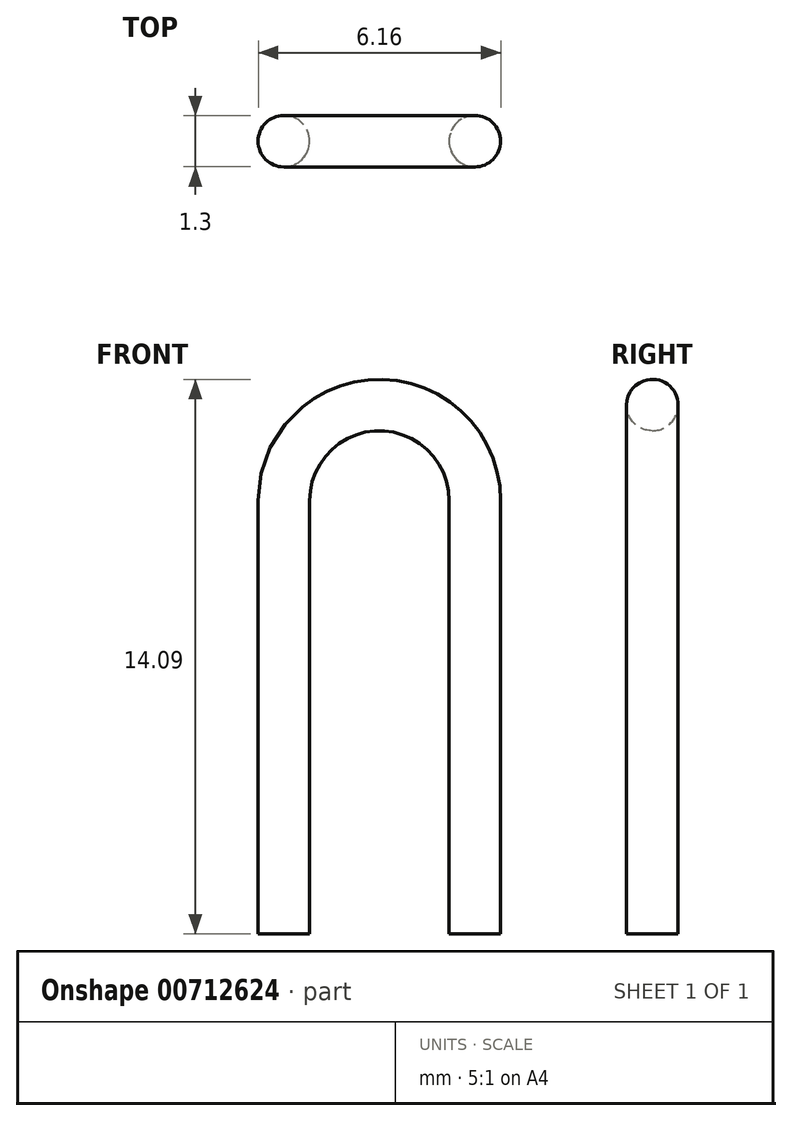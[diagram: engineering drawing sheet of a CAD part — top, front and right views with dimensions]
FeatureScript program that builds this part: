
annotation { "Feature Type Name" : "Feature", "Feature Type Description" : "" }
export const myFeature = defineFeature(function(context is Context, id is Id, definition is map)
    precondition{}
    {
        {
            var Q0;
            Q0=qCreatedBy(makeId("Front.planeOp"),FACE);
            var sketch = newSketch(context, id + "F0", { "sketchPlane" : qUnion([Q0])});
            skLineSegment(sketch, "E0", {"start": v(0, 0) * mm, "end": v(0, 11.01) * mm});
            skLineSegment(sketch, "E1", {"start": v(4.85, 0) * mm, "end": v(4.85, 11.01) * mm});
            skArc(sketch, "E2", {"start": v(4.85, 11.01) * mm, "mid": v(2.43, 13.44) * mm, "end": v(0, 11.01) * mm});
            skPoint(sketch, "E3", {"position": v(2.43, 13.44) * mm});
            skSolve(sketch);
        }
        {
            var Q0;
            Q0=sQuery(id+"F0.wireOp",VERTEX,"E0.start");
            var Q1;
            Q1=qCreatedBy(makeId("Top.planeOp"),FACE);
            cPlane(context, id + "F1", {"entities" : qUnion([Q0, Q1]), "cplaneType" : CPlaneType.PLANE_POINT, "offset" : 25.4 * mm, "width" : 152.4 * mm, "height" : 152.4 * mm});
        }
        {
            var Q0;
            Q0=qCreatedBy(id+"F1.planeOp",FACE);
            var sketch = newSketch(context, id + "F2", { "sketchPlane" : qUnion([Q0])});
            skCircle(sketch, "E4", {"center": v(0, 0) * mm, "radius": 0.65 * mm});
            skSolve(sketch);
        }
        {
            var Q0;
            Q0=makeQuery(id+"F2.imprint","IMPRINT",FACE,{"disambiguationData":[TD([[makeQuery(id+"F2.imprint","IMPRINT",EDGE,{"derivedFrom":sQuery(id+"F2.wireOp",EDGE,"E4")}),1.0]])]});
            var Q1;
            Q1=sQuery(id+"F0.wireOp",EDGE,"E0");
            var Q2;
            Q2=sQuery(id+"F0.wireOp",EDGE,"E1");
            var Q3;
            Q3=sQuery(id+"F0.wireOp",EDGE,"E2");
            sweep(context, id + "F3", {"profiles" : qUnion([Q0]), "path" : qUnion([Q1, Q2, Q3])});
        }
    });
